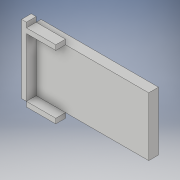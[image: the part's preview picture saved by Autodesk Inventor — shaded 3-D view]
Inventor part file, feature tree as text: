
AUTODESK INVENTOR PART (.ipt)
format: ipt  version: 2017 (Build 210142000, 142)  size: 130,048 bytes
history: native  units: in
note: dims shown in document units (in); Inventor stores cm internally (conversion verified against a paired STEP export)
features: sketch x6, extrude x5
ambient origin geometry x8: Origin, YZ Plane, XZ Plane, XY Plane, X Axis, Y Axis, Z Axis, Center Point
bodies: Solid1 (feature_tree)
feature tree (11):
  extrude  "Extrusion1"  Depth=6.0in
  extrude  "Extrusion2"  Depth=0.5in
  sketch  "Sketch3"  dims[d5=1.0in d6=0.0in d7=3.0in]
  extrude  "Extrusion3"  Depth=3.0in
  extrude  "Extrusion4"  Depth=0.5in TaperAngle=0.0deg
  sketch  "Sketch5"  dims[d11=0.5in d12=0.0in d13=1.0in d14=0.0in]
  extrude  "Extrusion5"  Depth=1.0in TaperAngle=0.0deg
  sketch  "Sketch1"  dims[d0=12.0in d1=6.0in]
  sketch  "Sketch2"  dims[d2=1.0in d3=0.0in d4=0.5in]
  sketch  "Sketch4"  dims[d8=3.0in d9=0.5in d10=0.0in]
  sketch  "Sketch6"
